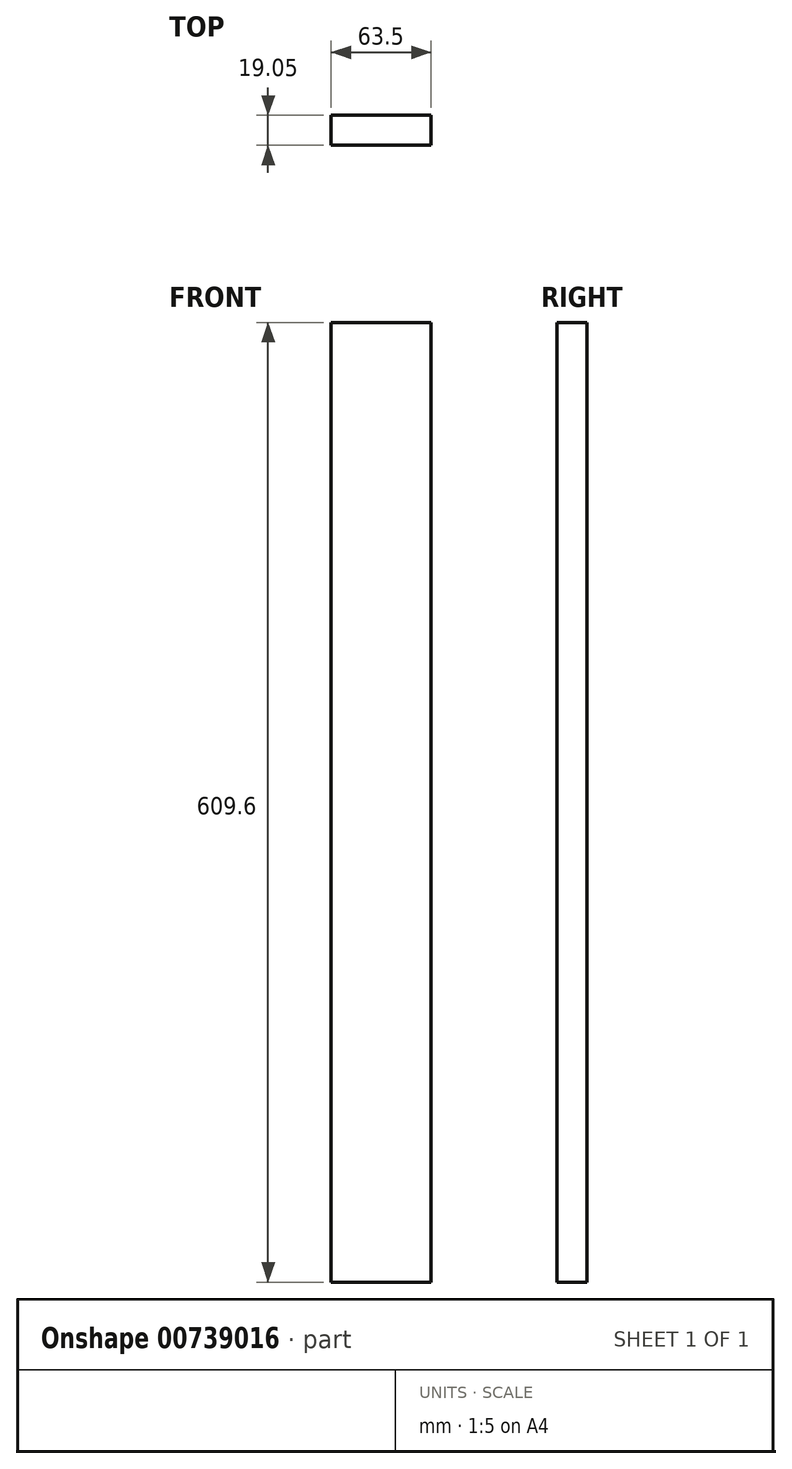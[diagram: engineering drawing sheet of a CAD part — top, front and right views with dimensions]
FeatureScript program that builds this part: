
annotation { "Feature Type Name" : "Feature", "Feature Type Description" : "" }
export const myFeature = defineFeature(function(context is Context, id is Id, definition is map)
    precondition{}
    {
        {
            var Q0;
            Q0=qCreatedBy(makeId("Front.planeOp"),FACE);
            var sketch = newSketch(context, id + "F0", { "sketchPlane" : qUnion([Q0])});
            skLineSegment(sketch, "E0.bottom", {"start": v(-81.8, 481.8) * mm, "end": v(-18.3, 481.8) * mm});
            skLineSegment(sketch, "E0.top", {"start": v(-81.8, -127.8) * mm, "end": v(-18.3, -127.8) * mm});
            skLineSegment(sketch, "E0.left", {"start": v(-81.8, 481.8) * mm, "end": v(-81.8, -127.8) * mm});
            skLineSegment(sketch, "E0.right", {"start": v(-18.3, 481.8) * mm, "end": v(-18.3, -127.8) * mm});
            skSolve(sketch);
        }
        {
            var Q0;
            Q0 = qSketchRegion(id + "F0", true);
            extrude(context, id + "F1", {"entities" : qUnion([Q0]), "depth" : 19.05 * mm, "offsetDistance" : 25.4 * mm});
        }
    });
